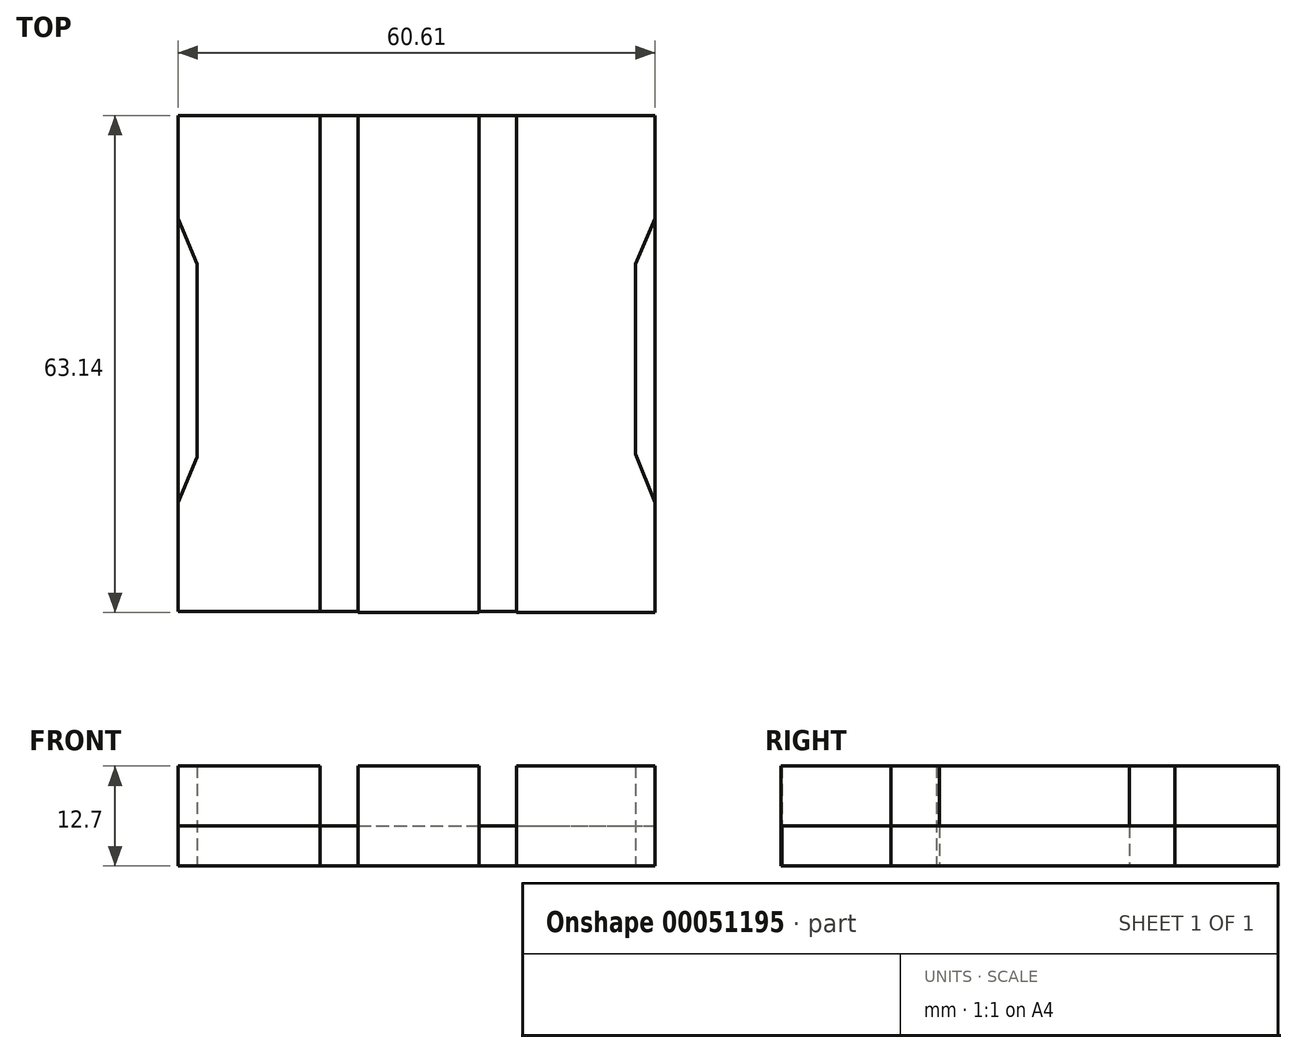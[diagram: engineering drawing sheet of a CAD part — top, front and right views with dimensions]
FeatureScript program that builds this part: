
annotation { "Feature Type Name" : "Feature", "Feature Type Description" : "" }
export const myFeature = defineFeature(function(context is Context, id is Id, definition is map)
    precondition{}
    {
        {
            var Q0;
            Q0=qCreatedBy(makeId("Top.planeOp"),FACE);
            var sketch = newSketch(context, id + "F0", { "sketchPlane" : qUnion([Q0])});
            skPoint(sketch, "E0", {"position": v(39.27, 69.9) * mm});
            skLineSegment(sketch, "E1", {"start": v(39.27, 69.9) * mm, "end": v(57.34, 69.9) * mm});
            skLineSegment(sketch, "E2", {"start": v(57.34, 69.9) * mm, "end": v(57.34, 6.87) * mm});
            skLineSegment(sketch, "E3", {"start": v(57.34, 6.87) * mm, "end": v(39.27, 6.87) * mm});
            skLineSegment(sketch, "E4", {"start": v(39.27, 6.87) * mm, "end": v(39.27, 20.73) * mm});
            skLineSegment(sketch, "E5", {"start": v(39.27, 20.73) * mm, "end": v(41.7, 26.5) * mm});
            skLineSegment(sketch, "E6", {"start": v(41.7, 26.5) * mm, "end": v(41.7, 51.02) * mm});
            skLineSegment(sketch, "E7", {"start": v(41.7, 51.02) * mm, "end": v(39.27, 56.8) * mm});
            skLineSegment(sketch, "E8", {"start": v(39.27, 56.8) * mm, "end": v(39.27, 69.9) * mm});
            skLineSegment(sketch, "E9", {"start": v(62.15, 69.9) * mm, "end": v(77.5, 69.9) * mm});
            skLineSegment(sketch, "E10", {"start": v(77.5, 69.9) * mm, "end": v(77.5, 6.76) * mm});
            skLineSegment(sketch, "E11", {"start": v(77.5, 6.76) * mm, "end": v(62.14, 6.76) * mm});
            skLineSegment(sketch, "E12", {"start": v(62.14, 6.76) * mm, "end": v(62.15, 69.9) * mm});
            skLineSegment(sketch, "E13", {"start": v(82.27, 69.9) * mm, "end": v(99.88, 69.9) * mm});
            skLineSegment(sketch, "E14", {"start": v(99.88, 69.9) * mm, "end": v(99.88, 56.8) * mm});
            skLineSegment(sketch, "E15", {"start": v(99.88, 56.8) * mm, "end": v(97.36, 51.02) * mm});
            skLineSegment(sketch, "E16", {"start": v(97.36, 51.02) * mm, "end": v(97.36, 26.88) * mm});
            skLineSegment(sketch, "E17", {"start": v(97.36, 26.88) * mm, "end": v(99.88, 20.73) * mm});
            skLineSegment(sketch, "E18", {"start": v(99.88, 20.73) * mm, "end": v(99.88, 6.76) * mm});
            skLineSegment(sketch, "E19", {"start": v(99.88, 6.76) * mm, "end": v(82.27, 6.76) * mm});
            skLineSegment(sketch, "E20", {"start": v(82.27, 6.76) * mm, "end": v(82.27, 69.9) * mm});
            skSolve(sketch);
        }
        {
            var Q0;
            Q0 = qSketchRegion(id + "F0", true);
            extrude(context, id + "F1", {"entities" : qUnion([Q0]), "depth" : 12.7 * mm});
        }
        {
            var Q0;
            Q0=makeQuery(id+"F1.opExtrude","CAP_FACE",FACE,{"disambiguationData":[OSD([sQuery(id+"F0.wireOp",EDGE,"E13"),sQuery(id+"F0.wireOp",EDGE,"E14"),sQuery(id+"F0.wireOp",EDGE,"E15"),sQuery(id+"F0.wireOp",EDGE,"E16"),sQuery(id+"F0.wireOp",EDGE,"E17"),sQuery(id+"F0.wireOp",EDGE,"E18"),sQuery(id+"F0.wireOp",EDGE,"E19"),sQuery(id+"F0.wireOp",EDGE,"E20")])],"isStart":true});
            var sketch = newSketch(context, id + "F2", { "sketchPlane" : qUnion([Q0])});
            skPoint(sketch, "E21", {"position": v(39.27, -6.87) * mm});
            skPoint(sketch, "E22", {"position": v(99.88, -69.9) * mm});
            skLineSegment(sketch, "E23.bottom", {"start": v(39.27, -6.87) * mm, "end": v(99.88, -6.87) * mm});
            skLineSegment(sketch, "E23.top", {"start": v(39.27, -69.9) * mm, "end": v(99.88, -69.9) * mm});
            skLineSegment(sketch, "E23.left", {"start": v(39.27, -6.87) * mm, "end": v(39.27, -69.9) * mm});
            skLineSegment(sketch, "E23.right", {"start": v(99.88, -6.87) * mm, "end": v(99.88, -69.9) * mm});
            skSolve(sketch);
        }
        {
            var Q0;
            Q0 = qSketchRegion(id + "F2", true);
            extrude(context, id + "F3", {"entities" : qUnion([Q0]), "oppositeDirection" : true, "depth" : 5.08 * mm});
        }
    });
